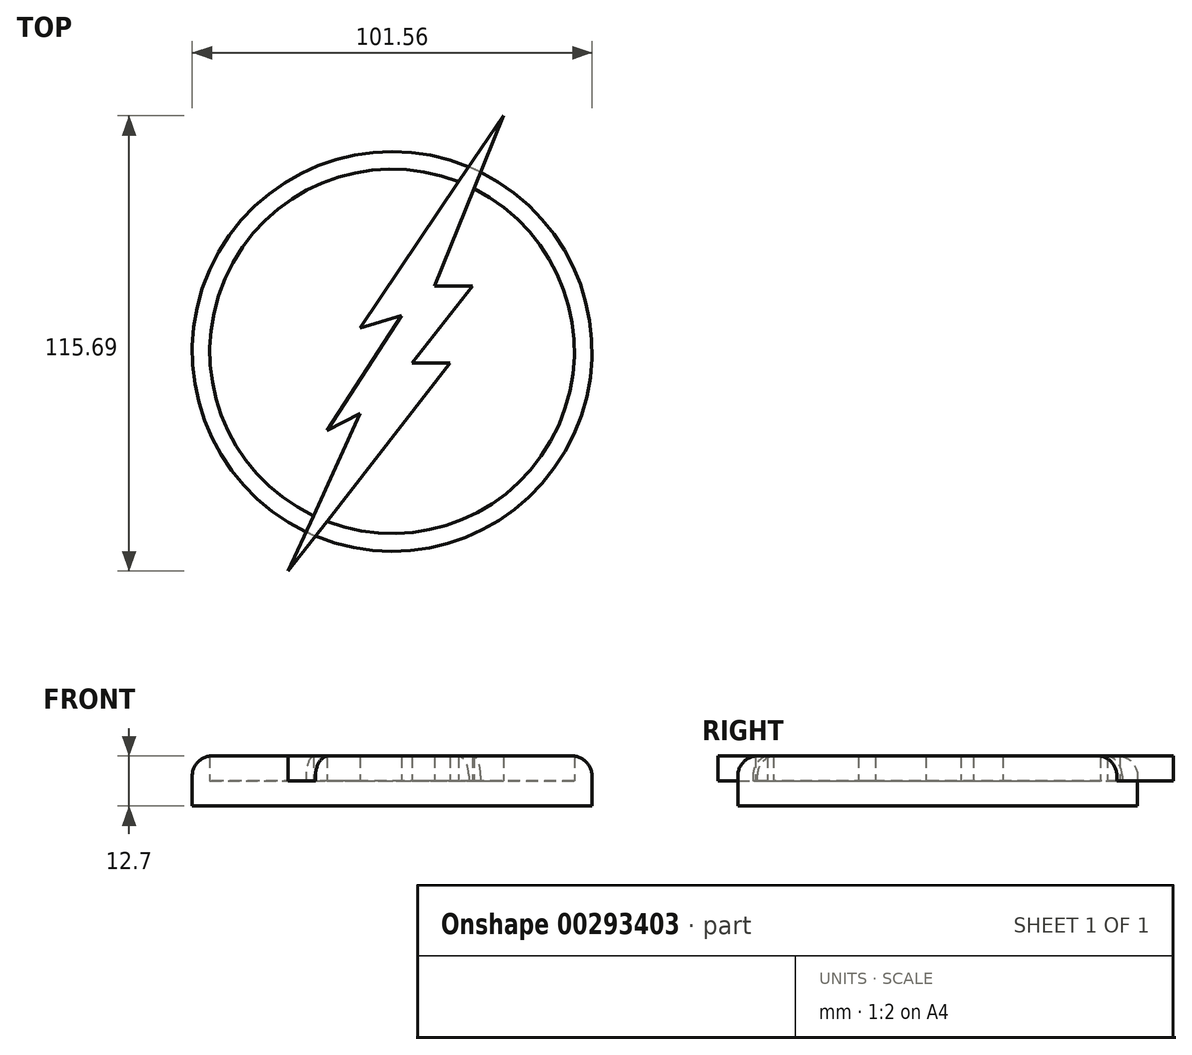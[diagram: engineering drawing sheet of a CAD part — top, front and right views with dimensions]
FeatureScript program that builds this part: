
annotation { "Feature Type Name" : "Feature", "Feature Type Description" : "" }
export const myFeature = defineFeature(function(context is Context, id is Id, definition is map)
    precondition{}
    {
        {
            var Q0;
            Q0=qCreatedBy(makeId("Top.planeOp"),FACE);
            var sketch = newSketch(context, id + "F0", { "sketchPlane" : qUnion([Q0])});
            skCircle(sketch, "E0", {"center": v(0, 0) * mm, "radius": 50.78 * mm});
            skCircle(sketch, "E1", {"center": v(0, 0) * mm, "radius": 46.3 * mm});
            skSolve(sketch);
        }
        {
            var Q0;
            Q0=makeQuery(id+"F0.imprint","IMPRINT",FACE,{"disambiguationData":[TD([[makeQuery(id+"F0.imprint","IMPRINT",EDGE,{"derivedFrom":sQuery(id+"F0.wireOp",EDGE,"E1")}),1.0]])]});
            extrude(context, id + "F1", {"entities" : qUnion([Q0]), "depth" : 6.35 * mm});
        }
        {
            var Q0;
            Q0=qSketchRegion(id+"F0",true);
            extrude(context, id + "F2", {"entities" : qUnion([Q0]), "operationType" : NewBodyOperationType.ADD, "depth" : 12.7 * mm});
        }
        {
            var Q0;
            Q0=makeQuery(id+"F2.opExtrude","CAP_EDGE",EDGE,{"disambiguationData":[OSD([sQuery(id+"F0.wireOp",EDGE,"E0")])],"isStart":false});
            fillet(context, id + "F3", {"entities" : qUnion([Q0]), "radius" : 5.08 * mm, "tangentPropagation" : true, "allowEdgeOverflow" : false});
        }
        {
            var Q0;
            Q0=makeQuery(id+"F1.opExtrude","CAP_FACE",FACE,{"disambiguationData":[OSD([sQuery(id+"F0.wireOp",EDGE,"E1")])],"isStart":false});
            var sketch = newSketch(context, id + "F4", { "sketchPlane" : qUnion([Q0])});
            skLineSegment(sketch, "E2", {"start": v(-26.37, -55.83) * mm, "end": v(14.74, -3) * mm});
            skLineSegment(sketch, "E3", {"start": v(14.74, -3) * mm, "end": v(5.11, -3) * mm});
            skLineSegment(sketch, "E4", {"start": v(5.11, -3) * mm, "end": v(20.4, 16.65) * mm});
            skLineSegment(sketch, "E5", {"start": v(20.4, 16.65) * mm, "end": v(10.83, 16.65) * mm});
            skLineSegment(sketch, "E6", {"start": v(10.83, 16.65) * mm, "end": v(28.27, 59.86) * mm});
            skLineSegment(sketch, "E7", {"start": v(-26.37, -55.83) * mm, "end": v(-8.18, -15.8) * mm});
            skLineSegment(sketch, "E8", {"start": v(-8.18, -15.8) * mm, "end": v(-16.54, -20.15) * mm});
            skLineSegment(sketch, "E9", {"start": v(-16.54, -20.15) * mm, "end": v(2.4, 9.1) * mm});
            skLineSegment(sketch, "E10", {"start": v(-8.18, 5.94) * mm, "end": v(28.27, 59.86) * mm});
            skLineSegment(sketch, "E11", {"start": v(-8.18, 5.94) * mm, "end": v(2.4, 9.1) * mm});
            skSolve(sketch);
        }
        {
            var Q0;
            Q0=qSketchRegion(id+"F4",true);
            extrude(context, id + "F5", {"entities" : qUnion([Q0]), "operationType" : NewBodyOperationType.ADD, "depth" : 6.35 * mm});
        }
    });
